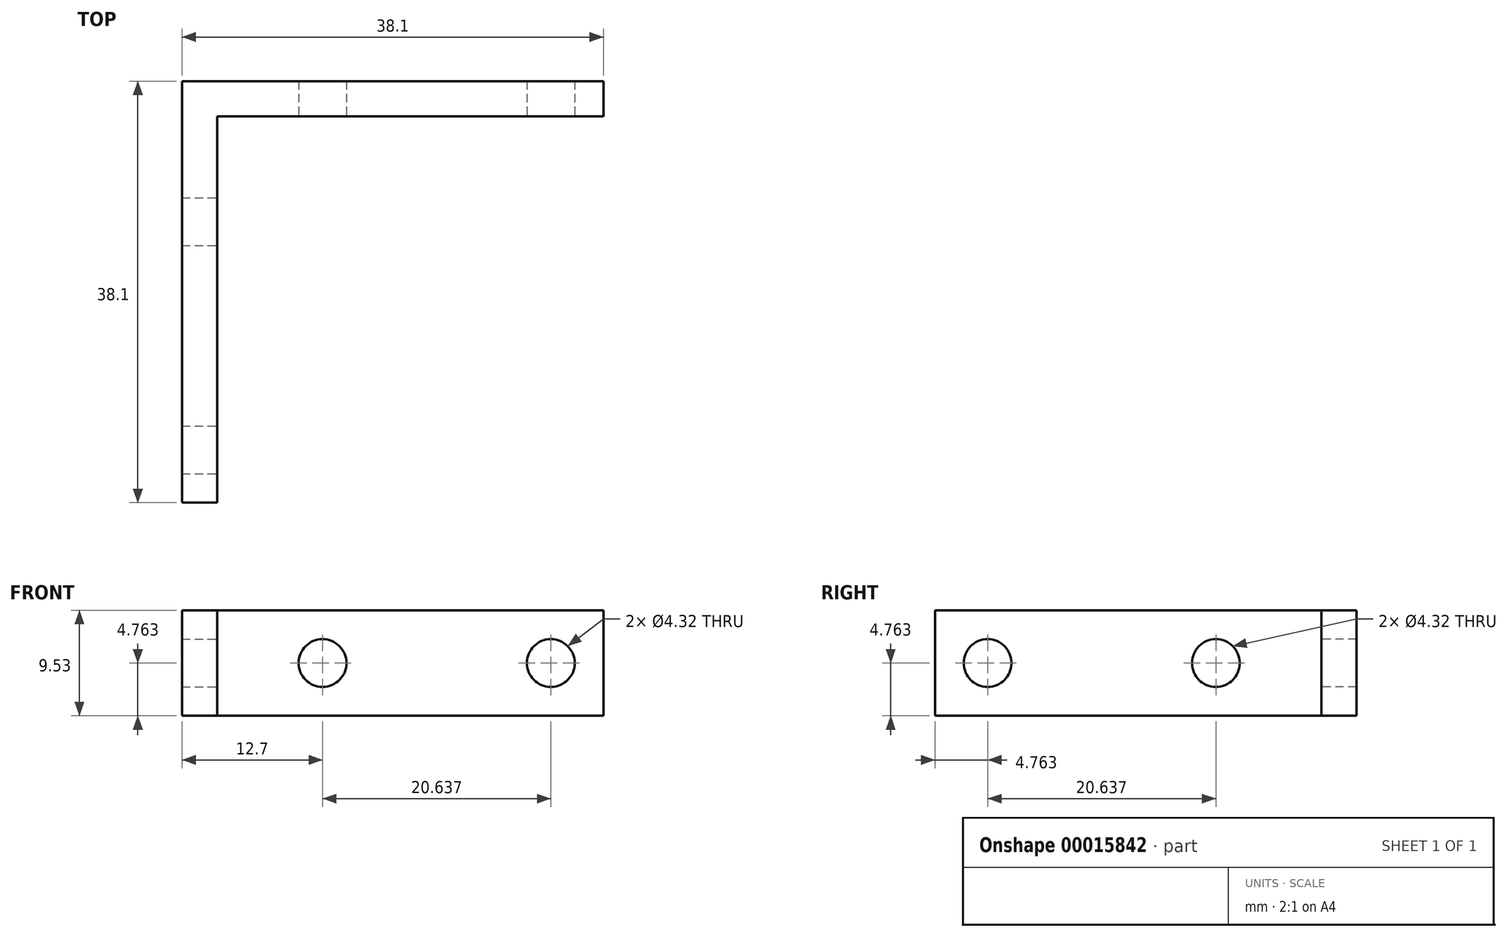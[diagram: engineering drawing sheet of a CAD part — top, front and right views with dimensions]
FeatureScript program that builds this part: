
annotation { "Feature Type Name" : "Feature", "Feature Type Description" : "" }
export const myFeature = defineFeature(function(context is Context, id is Id, definition is map)
    precondition{}
    {
        {
            var Q0;
            Q0=qCreatedBy(makeId("Top.planeOp"),FACE);
            var sketch = newSketch(context, id + "F0", { "sketchPlane" : qUnion([Q0])});
            skLineSegment(sketch, "E0.bottom", {"start": v(0, 0) * mm, "end": v(38.1, 0) * mm});
            skLineSegment(sketch, "E0.left", {"start": v(0, 0) * mm, "end": v(0, -38.1) * mm});
            skLineSegment(sketch, "E1.top", {"start": v(38.1, -3.17) * mm, "end": v(3.18, -3.18) * mm});
            skLineSegment(sketch, "E1.right", {"start": v(3.18, -38.1) * mm, "end": v(3.18, -3.18) * mm});
            skLineSegment(sketch, "E2", {"start": v(0, -38.1) * mm, "end": v(3.18, -38.1) * mm});
            skLineSegment(sketch, "E3", {"start": v(38.1, -3.18) * mm, "end": v(38.1, 0) * mm});
            skSolve(sketch);
        }
        {
            var Q0;
            Q0 = qSketchRegion(id + "F0", true);
            extrude(context, id + "F1", {"entities" : qUnion([Q0]), "depth" : 9.52 * mm});
        }
        {
            var Q0;
            Q0=makeQuery(id+"F1.opExtrude","SWEPT_FACE",FACE,{"disambiguationData":[OSD([sQuery(id+"F0.wireOp",EDGE,"E1.top")])]});
            var sketch = newSketch(context, id + "F2", { "sketchPlane" : qUnion([Q0])});
            skLineSegment(sketch, "E4", {"start": v(38.1, 4.76) * mm, "end": v(33.34, 4.76) * mm});
            skLineSegment(sketch, "E5", {"start": v(33.34, 4.76) * mm, "end": v(33.34, 9.53) * mm});
            skCircle(sketch, "E6", {"center": v(33.34, 4.76) * mm, "radius": 2.16 * mm});
            skLineSegment(sketch, "E7", {"start": v(3.18, 4.76) * mm, "end": v(12.7, 4.76) * mm});
            skCircle(sketch, "E8", {"center": v(12.7, 4.76) * mm, "radius": 2.16 * mm});
            skSolve(sketch);
        }
        {
            var Q0;
            Q0 = qSketchRegion(id + "F2", true);
            extrude(context, id + "F3", {"entities" : qUnion([Q0]), "operationType" : NewBodyOperationType.REMOVE, "oppositeDirection" : true, "depth" : 25.4 * mm});
        }
        {
            var Q0;
            Q0=makeQuery(id+"F1.opExtrude","SWEPT_FACE",FACE,{"disambiguationData":[OSD([sQuery(id+"F0.wireOp",EDGE,"E1.right")])]});
            var sketch = newSketch(context, id + "F4", { "sketchPlane" : qUnion([Q0])});
            skLineSegment(sketch, "E9", {"start": v(-38.1, 4.76) * mm, "end": v(-33.34, 4.76) * mm});
            skLineSegment(sketch, "E10", {"start": v(-33.34, 4.76) * mm, "end": v(-33.34, 9.53) * mm});
            skCircle(sketch, "E11", {"center": v(-33.34, 4.76) * mm, "radius": 2.16 * mm});
            skLineSegment(sketch, "E12", {"start": v(-3.18, 4.76) * mm, "end": v(-12.7, 4.76) * mm});
            skCircle(sketch, "E13", {"center": v(-12.7, 4.76) * mm, "radius": 2.16 * mm});
            skSolve(sketch);
        }
        {
            var Q0;
            Q0 = qSketchRegion(id + "F4", true);
            extrude(context, id + "F5", {"entities" : qUnion([Q0]), "operationType" : NewBodyOperationType.REMOVE, "oppositeDirection" : true, "depth" : 25.4 * mm});
        }
    });
